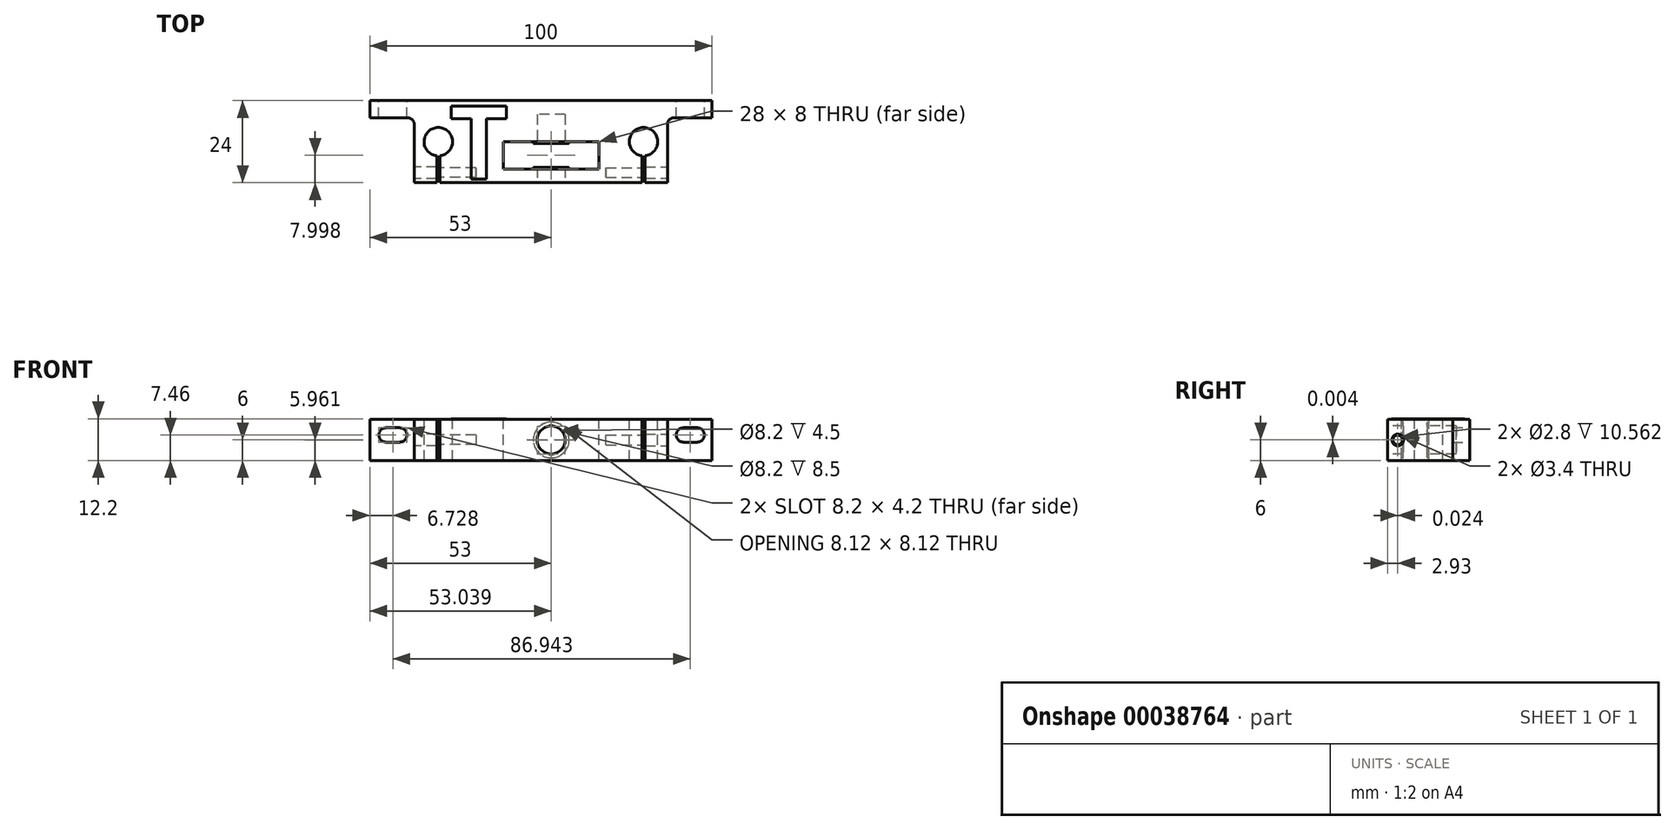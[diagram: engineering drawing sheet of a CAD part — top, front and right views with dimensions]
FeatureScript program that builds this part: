
annotation { "Feature Type Name" : "Feature", "Feature Type Description" : "" }
export const myFeature = defineFeature(function(context is Context, id is Id, definition is map)
    precondition{}
    {
        {
            var Q0;
            Q0=qCreatedBy(makeId("Top.planeOp"),FACE);
            var sketch = newSketch(context, id + "F0", { "sketchPlane" : qUnion([Q0])});
            skLineSegment(sketch, "E0", {"start": v(-46.35, 12.3) * mm, "end": v(53.65, 12.3) * mm});
            skLineSegment(sketch, "E1", {"start": v(53.65, 12.3) * mm, "end": v(53.65, 7.3) * mm});
            skLineSegment(sketch, "E2", {"start": v(53.65, 7.3) * mm, "end": v(40.65, 7.3) * mm});
            skLineSegment(sketch, "E3", {"start": v(40.65, 7.3) * mm, "end": v(40.65, -11.7) * mm});
            skLineSegment(sketch, "E4", {"start": v(40.65, -11.7) * mm, "end": v(-33.35, -11.7) * mm});
            skLineSegment(sketch, "E5", {"start": v(-33.35, -11.7) * mm, "end": v(-33.35, 7.3) * mm});
            skLineSegment(sketch, "E6", {"start": v(-33.35, 7.3) * mm, "end": v(-46.35, 7.3) * mm});
            skLineSegment(sketch, "E7", {"start": v(-46.35, 7.3) * mm, "end": v(-46.35, 12.3) * mm});
            skSolve(sketch);
        }
        {
            var Q0;
            Q0=qSketchRegion(id+"F0",true);
            extrude(context, id + "F1", {"entities" : qUnion([Q0]), "depth" : 12 * mm});
        }
        {
            var Q0;
            Q0=makeQuery(id+"F1.opExtrude","CAP_FACE",FACE,{"disambiguationData":[OSD([sQuery(id+"F0.wireOp",EDGE,"E0"),sQuery(id+"F0.wireOp",EDGE,"E1"),sQuery(id+"F0.wireOp",EDGE,"E2"),sQuery(id+"F0.wireOp",EDGE,"E3"),sQuery(id+"F0.wireOp",EDGE,"E4"),sQuery(id+"F0.wireOp",EDGE,"E5"),sQuery(id+"F0.wireOp",EDGE,"E6"),sQuery(id+"F0.wireOp",EDGE,"E7")])],"isStart":false});
            var sketch = newSketch(context, id + "F2", { "sketchPlane" : qUnion([Q0])});
            skCircle(sketch, "E8", {"center": v(-26.35, 0.3) * mm, "radius": 4.15 * mm});
            skCircle(sketch, "E9", {"center": v(33.65, 0.3) * mm, "radius": 4.15 * mm});
            skPoint(sketch, "E10", {"position": v(3.65, 12.3) * mm});
            skLineSegment(sketch, "E11.bottom", {"start": v(33.21, -3.01) * mm, "end": v(34.09, -3.01) * mm});
            skLineSegment(sketch, "E11.top", {"start": v(33.21, -12.27) * mm, "end": v(34.09, -12.27) * mm});
            skLineSegment(sketch, "E11.left", {"start": v(33.21, -3.01) * mm, "end": v(33.21, -12.27) * mm});
            skLineSegment(sketch, "E11.right", {"start": v(34.09, -3.01) * mm, "end": v(34.09, -12.27) * mm});
            skPoint(sketch, "E12", {"position": v(33.65, -3.01) * mm});
            skLineSegment(sketch, "E13", {"start": v(3.65, 12.3) * mm, "end": v(3.65, -11.7) * mm, "construction": true});
            skLineSegment(sketch, "E14.MirrorCS", {"start": v(-25.91, -12.27) * mm, "end": v(-26.79, -12.27) * mm});
            skLineSegment(sketch, "E15.MirrorCS", {"start": v(-26.79, -3.01) * mm, "end": v(-26.79, -12.27) * mm});
            skLineSegment(sketch, "E16.MirrorCS", {"start": v(-25.91, -3.01) * mm, "end": v(-26.79, -3.01) * mm});
            skLineSegment(sketch, "E17.MirrorCS", {"start": v(-25.91, -3.01) * mm, "end": v(-25.91, -12.27) * mm});
            skSolve(sketch);
        }
        {
            var Q0;
            Q0=qSketchRegion(id+"F2",true);
            var Q1;
            {var subQ3=sQuery(id+"F2.wireOp",EDGE,"E11.bottom");Q1=makeQuery(id+"F2.imprint","IMPRINT",FACE,{"disambiguationData":[TD([[makeQuery(id+"F2.imprint","IMPRINT",EDGE,{"derivedFrom":subQ3}),-1.0]])]});}
            var Q2;
            {var subQ3=sQuery(id+"F2.wireOp",EDGE,"E16.MirrorCS");Q2=makeQuery(id+"F2.imprint","IMPRINT",FACE,{"disambiguationData":[TD([[makeQuery(id+"F2.imprint","IMPRINT",EDGE,{"derivedFrom":subQ3}),1.0]])]});}
            extrude(context, id + "F3", {"entities" : qUnion([Q0, Q1, Q2]), "operationType" : NewBodyOperationType.REMOVE, "endBound" : BoundingType.THROUGH_ALL, "oppositeDirection" : true, "depth" : 25 * mm});
        }
        {
            var Q0;
            Q0=makeQuery(id+"F1.opExtrude","SWEPT_FACE",FACE,{"disambiguationData":[OSD([sQuery(id+"F0.wireOp",EDGE,"E0")])]});
            var sketch = newSketch(context, id + "F4", { "sketchPlane" : qUnion([Q0])});
            skLineSegment(sketch, "E18", {"start": v(-53.65, 7.46) * mm, "end": v(46.35, 7.46) * mm, "construction": true});
            skLineSegment(sketch, "E19.bottom", {"start": v(-49.32, 9.56) * mm, "end": v(-45.32, 9.56) * mm});
            skLineSegment(sketch, "E19.top", {"start": v(-49.32, 5.36) * mm, "end": v(-45.32, 5.36) * mm});
            skArc(sketch, "E20", {"start": v(-45.32, 5.36) * mm, "mid": v(-43.22, 7.46) * mm, "end": v(-45.32, 9.56) * mm});
            skArc(sketch, "E21", {"start": v(-49.32, 9.56) * mm, "mid": v(-51.42, 7.46) * mm, "end": v(-49.32, 5.36) * mm});
            skLineSegment(sketch, "E22.top", {"start": v(37.62, 5.36) * mm, "end": v(41.62, 5.36) * mm});
            skLineSegment(sketch, "E22.bottom", {"start": v(37.62, 9.56) * mm, "end": v(41.62, 9.56) * mm});
            skArc(sketch, "E23", {"start": v(37.62, 9.56) * mm, "mid": v(35.52, 7.46) * mm, "end": v(37.62, 5.36) * mm});
            skArc(sketch, "E24", {"start": v(41.62, 5.36) * mm, "mid": v(43.72, 7.46) * mm, "end": v(41.62, 9.56) * mm});
            skSolve(sketch);
        }
        {
            var Q0;
            Q0=qSketchRegion(id+"F4",true);
            extrude(context, id + "F5", {"entities" : qUnion([Q0]), "operationType" : NewBodyOperationType.REMOVE, "endBound" : BoundingType.THROUGH_ALL, "oppositeDirection" : true, "depth" : 25 * mm});
        }
        {
            var Q0;
            Q0=makeQuery(id+"F1.opExtrude","SWEPT_FACE",FACE,{"disambiguationData":[OSD([sQuery(id+"F0.wireOp",EDGE,"E4")])]});
            var sketch = newSketch(context, id + "F6", { "sketchPlane" : qUnion([Q0])});
            skLineSegment(sketch, "E25", {"start": v(-33.35, 6) * mm, "end": v(40.65, 6) * mm, "construction": true});
            skCircle(sketch, "E26", {"center": v(6.65, 6) * mm, "radius": 4.1 * mm});
            skSolve(sketch);
        }
        {
            var Q0;
            Q0=qSketchRegion(id+"F6",true);
            extrude(context, id + "F7", {"entities" : qUnion([Q0]), "operationType" : NewBodyOperationType.REMOVE, "oppositeDirection" : true, "depth" : 20 * mm});
        }
        {
            var Q0;
            Q0=makeQuery(id+"F1.opExtrude","CAP_FACE",FACE,{"disambiguationData":[OSD([sQuery(id+"F0.wireOp",EDGE,"E0"),sQuery(id+"F0.wireOp",EDGE,"E1"),sQuery(id+"F0.wireOp",EDGE,"E2"),sQuery(id+"F0.wireOp",EDGE,"E3"),sQuery(id+"F0.wireOp",EDGE,"E4"),sQuery(id+"F0.wireOp",EDGE,"E5"),sQuery(id+"F0.wireOp",EDGE,"E6"),sQuery(id+"F0.wireOp",EDGE,"E7")])],"isStart":false});
            var sketch = newSketch(context, id + "F8", { "sketchPlane" : qUnion([Q0])});
            skLineSegment(sketch, "E27.bottom", {"start": v(-7.35, 0.3) * mm, "end": v(20.65, 0.3) * mm});
            skLineSegment(sketch, "E27.top", {"start": v(-7.35, -7.7) * mm, "end": v(20.65, -7.7) * mm});
            skLineSegment(sketch, "E27.left", {"start": v(-7.35, 0.3) * mm, "end": v(-7.35, -7.7) * mm});
            skLineSegment(sketch, "E27.right", {"start": v(20.65, 0.3) * mm, "end": v(20.65, -7.7) * mm});
            skLineSegment(sketch, "E28", {"start": v(6.65, 12.3) * mm, "end": v(6.65, -11.7) * mm, "construction": true});
            skLineSegment(sketch, "E29", {"start": v(6.65, 0.3) * mm, "end": v(6.65, -7.7) * mm});
            skSolve(sketch);
        }
        {
            var Q0;
            Q0=qSketchRegion(id+"F8",true);
            extrude(context, id + "F9", {"entities" : qUnion([Q0]), "operationType" : NewBodyOperationType.REMOVE, "endBound" : BoundingType.THROUGH_ALL, "oppositeDirection" : true, "depth" : 25 * mm});
        }
        {
            var Q0;
            Q0=makeQuery(id+"F9.boolean.opBoolean","COPY",FACE,{"derivedFrom":makeQuery(id+"F9.opExtrude","SWEPT_FACE",FACE,{"disambiguationData":[OSD([sQuery(id+"F8.wireOp",EDGE,"E27.bottom")])]})});
            var sketch = newSketch(context, id + "F10", { "sketchPlane" : qUnion([Q0])});
            skCircle(sketch, "E30", {"center": v(6.65, 6) * mm, "radius": 5.2 * mm});
            skSolve(sketch);
        }
        {
            var Q0;
            Q0=makeQuery(id+"F10.imprint","IMPRINT",FACE,{"disambiguationData":[TD([[makeQuery(id+"F10.imprint","IMPRINT",EDGE,{"derivedFrom":sQuery(id+"F10.wireOp",EDGE,"E30")}),1.0]])]});
            extrude(context, id + "F11", {"entities" : qUnion([Q0]), "operationType" : NewBodyOperationType.ADD, "depth" : 0.5 * mm});
        }
        {
            var Q0;
            Q0=makeQuery(id+"F9.boolean.opBoolean","COPY",FACE,{"derivedFrom":makeQuery(id+"F9.opExtrude","SWEPT_FACE",FACE,{"disambiguationData":[OSD([sQuery(id+"F8.wireOp",EDGE,"E27.top")])]})});
            var sketch = newSketch(context, id + "F12", { "sketchPlane" : qUnion([Q0])});
            skCircle(sketch, "E31", {"center": v(-6.65, 6) * mm, "radius": 5.25 * mm});
            skSolve(sketch);
        }
        {
            var Q0;
            Q0=makeQuery(id+"F12.imprint","IMPRINT",FACE,{"disambiguationData":[TD([[makeQuery(id+"F12.imprint","IMPRINT",EDGE,{"derivedFrom":sQuery(id+"F12.wireOp",EDGE,"E31")}),1.0]])]});
            extrude(context, id + "F13", {"entities" : qUnion([Q0]), "operationType" : NewBodyOperationType.ADD, "depth" : 0.5 * mm});
        }
        {
            var Q0;
            Q0=makeQuery(id+"F1.opExtrude","CAP_FACE",FACE,{"disambiguationData":[OSD([sQuery(id+"F0.wireOp",EDGE,"E0"),sQuery(id+"F0.wireOp",EDGE,"E1"),sQuery(id+"F0.wireOp",EDGE,"E2"),sQuery(id+"F0.wireOp",EDGE,"E3"),sQuery(id+"F0.wireOp",EDGE,"E4"),sQuery(id+"F0.wireOp",EDGE,"E5"),sQuery(id+"F0.wireOp",EDGE,"E6"),sQuery(id+"F0.wireOp",EDGE,"E7")])],"isStart":false});
            var sketch = newSketch(context, id + "F14", { "sketchPlane" : qUnion([Q0])});
            skText(sketch, "E32", { "text": "T", "fontName": "OpenSans-Bold.ttf"});
            const initialGuessF14  = {"E32": [-0.02318, -0.01058, 1, 0, 0.0215]};
            skSetInitialGuess(sketch, initialGuessF14);
            skSolve(sketch);
        }
        {
            var Q0;
            Q0=makeQuery(id+"F14.imprint","IMPRINT",FACE,{"disambiguationData":[TD([[makeQuery(id+"F14.imprint","IMPRINT",EDGE,{"derivedFrom":sQuery(id+"F14.wireOp",EDGE,"E32.sketch_text.stroke-0")}),-1.0]])]});
            extrude(context, id + "F15", {"entities" : qUnion([Q0]), "operationType" : NewBodyOperationType.ADD, "depth" : .2 * mm});
        }
        {
            var Q0;
            Q0=makeQuery(id+"F1.opExtrude","SWEPT_FACE",FACE,{"disambiguationData":[OSD([sQuery(id+"F0.wireOp",EDGE,"E3")])]});
            var sketch = newSketch(context, id + "F16", { "sketchPlane" : qUnion([Q0])});
            skCircle(sketch, "E33", {"center": v(-8.74, 6) * mm, "radius": 1.7 * mm});
            skCircle(sketch, "E34", {"center": v(-8.74, 6) * mm, "radius": 1.4 * mm});
            skLineSegment(sketch, "E35", {"start": v(-11.7, 6) * mm, "end": v(-3.84, 6) * mm, "construction": true});
            skSolve(sketch);
        }
        {
            var Q0;
            Q0=makeQuery(id+"F16.imprint","IMPRINT",FACE,{"disambiguationData":[TD([[makeQuery(id+"F16.imprint","IMPRINT",EDGE,{"derivedFrom":sQuery(id+"F16.wireOp",EDGE,"E34")}),1.0]])]});
            extrude(context, id + "F17", {"entities" : qUnion([Q0]), "operationType" : NewBodyOperationType.REMOVE, "oppositeDirection" : true, "depth" : 18 * mm});
        }
        {
            var Q0;
            Q0=makeQuery(id+"F16.imprint","IMPRINT",FACE,{"disambiguationData":[TD([[makeQuery(id+"F16.imprint","IMPRINT",EDGE,{"derivedFrom":sQuery(id+"F16.wireOp",EDGE,"E34")}),1.0]])]});
            var Q1;
            Q1=makeQuery(id+"F16.imprint","IMPRINT",FACE,{"disambiguationData":[TD([[makeQuery(id+"F16.imprint","IMPRINT",EDGE,{"derivedFrom":sQuery(id+"F16.wireOp",EDGE,"E33")}),1.0]])]});
            extrude(context, id + "F18", {"entities" : qUnion([Q0, Q1]), "operationType" : NewBodyOperationType.REMOVE, "endBound" : BoundingType.UP_TO_NEXT, "oppositeDirection" : true, "depth" : 7 * mm});
        }
        {
            var Q0;
            Q0=makeQuery(id+"F1.opExtrude","SWEPT_EDGE",EDGE,{"disambiguationData":[OSD([sQuery(id+"F0.wireOp",EDGE,"E2"),sQuery(id+"F0.wireOp",EDGE,"E3")])]});
            fillet(context, id + "F19", {"entities" : qUnion([Q0]), "radius" : 2 * mm, "tangentPropagation" : true, "allowEdgeOverflow" : false});
        }
        {
            var Q0;
            Q0=makeQuery(id+"F1.opExtrude","SWEPT_FACE",FACE,{"disambiguationData":[OSD([sQuery(id+"F0.wireOp",EDGE,"E5")])]});
            var sketch = newSketch(context, id + "F20", { "sketchPlane" : qUnion([Q0])});
            skCircle(sketch, "E36", {"center": v(8.76, 6) * mm, "radius": 1.7 * mm});
            skCircle(sketch, "E37", {"center": v(8.76, 6) * mm, "radius": 1.4 * mm});
            skLineSegment(sketch, "E38", {"start": v(8.76, 0) * mm, "end": v(8.76, 12) * mm, "construction": true});
            skSolve(sketch);
        }
        {
            var Q0;
            Q0=makeQuery(id+"F20.imprint","IMPRINT",FACE,{"disambiguationData":[TD([[makeQuery(id+"F20.imprint","IMPRINT",EDGE,{"derivedFrom":sQuery(id+"F20.wireOp",EDGE,"E37")}),1.0]])]});
            extrude(context, id + "F21", {"entities" : qUnion([Q0]), "operationType" : NewBodyOperationType.REMOVE, "oppositeDirection" : true, "depth" : 18 * mm});
        }
        {
            var Q0;
            Q0=makeQuery(id+"F20.imprint","IMPRINT",FACE,{"disambiguationData":[TD([[makeQuery(id+"F20.imprint","IMPRINT",EDGE,{"derivedFrom":sQuery(id+"F20.wireOp",EDGE,"E37")}),1.0]])]});
            var Q1;
            Q1=makeQuery(id+"F20.imprint","IMPRINT",FACE,{"disambiguationData":[TD([[makeQuery(id+"F20.imprint","IMPRINT",EDGE,{"derivedFrom":sQuery(id+"F20.wireOp",EDGE,"E36")}),1.0]])]});
            extrude(context, id + "F22", {"entities" : qUnion([Q0, Q1]), "operationType" : NewBodyOperationType.REMOVE, "endBound" : BoundingType.UP_TO_NEXT, "oppositeDirection" : true, "depth" : 25 * mm});
        }
        {
            var Q0;
            Q0=makeQuery(id+"F1.opExtrude","SWEPT_EDGE",EDGE,{"disambiguationData":[OSD([sQuery(id+"F0.wireOp",EDGE,"E5"),sQuery(id+"F0.wireOp",EDGE,"E6")])]});
            fillet(context, id + "F23", {"entities" : qUnion([Q0]), "radius" : 2 * mm, "tangentPropagation" : true, "allowEdgeOverflow" : false});
        }
    });
